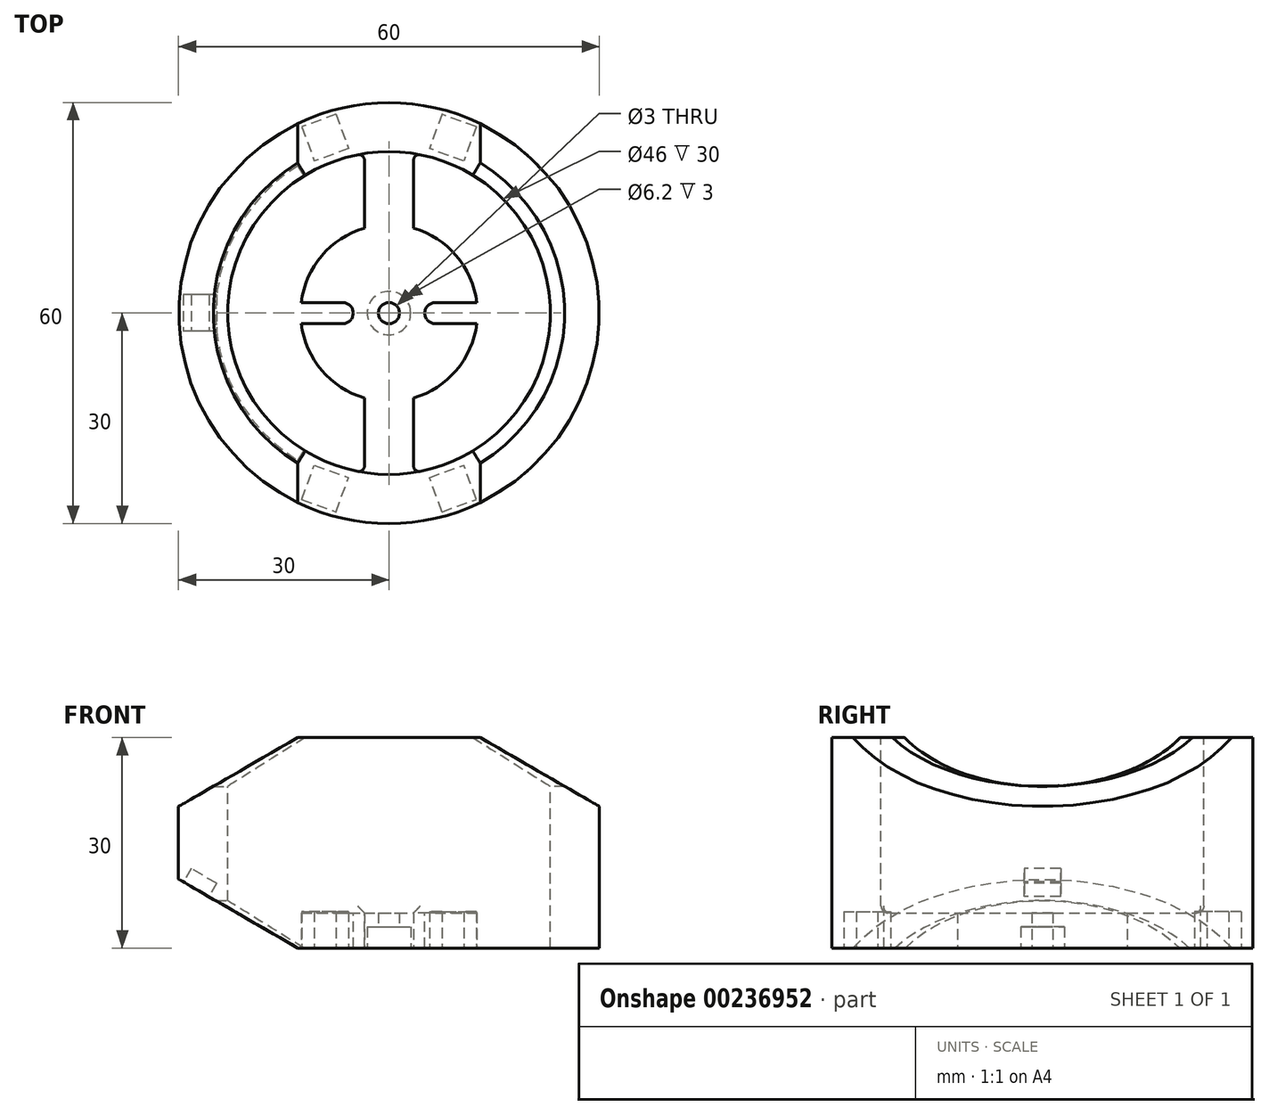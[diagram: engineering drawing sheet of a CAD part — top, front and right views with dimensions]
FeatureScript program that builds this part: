
annotation { "Feature Type Name" : "Feature", "Feature Type Description" : "" }
export const myFeature = defineFeature(function(context is Context, id is Id, definition is map)
    precondition{}
    {
        {
            var Q0;
            Q0=qCreatedBy(makeId("Top.planeOp"),FACE);
            var sketch = newSketch(context, id + "F0", { "sketchPlane" : qUnion([Q0])});
            skCircle(sketch, "E0", {"center": v(0, 0) * mm, "radius": 30 * mm});
            skSolve(sketch);
        }
        {
            var Q0;
            Q0 = qSketchRegion(id + "F0", true);
            extrude(context, id + "F1", {"entities" : qUnion([Q0]), "depth" : 30 * mm});
        }
        {
            var Q0;
            Q0=qCreatedBy(makeId("Front.planeOp"),FACE);
            var sketch = newSketch(context, id + "F2", { "sketchPlane" : qUnion([Q0])});
            skLineSegment(sketch, "E1", {"start": v(-30, 0) * mm, "end": v(-30, 30) * mm});
            skLineSegment(sketch, "E2.0", {"start": v(-30, 0) * mm, "end": v(30, 0) * mm});
            skLineSegment(sketch, "E3", {"start": v(-30, 9.81) * mm, "end": v(-13, 0) * mm});
            skSolve(sketch);
        }
        {
            var Q0;
            Q0 = qSketchRegion(id + "F2", true);
            extrude(context, id + "F3", {"entities" : qUnion([Q0]), "operationType" : NewBodyOperationType.REMOVE, "oppositeDirection" : true, "depth" : 40 * mm, "hasSecondDirection" : true, "secondDirectionOppositeDirection" : false, "secondDirectionDepth" : 40 * mm});
        }
        {
            var Q0;
            Q0=makeQuery(id+"F1.opExtrude","CAP_FACE",FACE,{"disambiguationData":[OSD([sQuery(id+"F0.wireOp",EDGE,"E0")])],"isStart":false});
            var sketch = newSketch(context, id + "F4", { "sketchPlane" : qUnion([Q0])});
            skCircle(sketch, "E4", {"center": v(0, 0) * mm, "radius": 23 * mm});
            skSolve(sketch);
        }
        {
            var Q0;
            Q0 = qSketchRegion(id + "F4", true);
            extrude(context, id + "F5", {"entities" : qUnion([Q0]), "operationType" : NewBodyOperationType.REMOVE, "oppositeDirection" : true, "depth" : 40 * mm});
        }
        {
            var Q0;
            Q0=makeQuery(id+"F5.boolean.opBoolean","SPLIT",FACE,{"disambiguationData":[OD(0.0)],"derivedFrom":makeQuery(id+"F1.opExtrude","CAP_FACE",FACE,{"disambiguationData":[OSD([sQuery(id+"F0.wireOp",EDGE,"E0")])],"isStart":true})});
            var sketch = newSketch(context, id + "F6", { "sketchPlane" : qUnion([Q0])});
            skCircle(sketch, "E5", {"center": v(0, 0) * mm, "radius": 12.6 * mm});
            skLineSegment(sketch, "E6.bottom", {"start": v(3.5, 25) * mm, "end": v(-3.5, 25) * mm});
            skLineSegment(sketch, "E6.top", {"start": v(3.5, -25) * mm, "end": v(-3.5, -25) * mm});
            skLineSegment(sketch, "E6.left", {"start": v(3.5, 25) * mm, "end": v(3.5, -25) * mm});
            skLineSegment(sketch, "E6.right", {"start": v(-3.5, 25) * mm, "end": v(-3.5, -25) * mm});
            skSolve(sketch);
        }
        {
            var Q0;
            Q0 = qSketchRegion(id + "F6", true);
            extrude(context, id + "F7", {"entities" : qUnion([Q0]), "operationType" : NewBodyOperationType.ADD, "oppositeDirection" : true, "depth" : 5 * mm});
        }
        {
            var Q0;
            {var subQ0=makeQuery(id+"F1.opExtrude","CAP_FACE",FACE,{"disambiguationData":[OSD([sQuery(id+"F0.wireOp",EDGE,"E0")])],"isStart":true});Q0=makeQuery(id+"F7.boolean.opBoolean","MERGE",FACE,{"derivedFrom":[makeQuery(id+"F5.boolean.opBoolean","SPLIT",FACE,{"disambiguationData":[OD(0.0)],"derivedFrom":subQ0}),makeQuery(id+"F5.boolean.opBoolean","SPLIT",FACE,{"disambiguationData":[OD(1.0)],"derivedFrom":subQ0}),makeQuery(id+"F7.opExtrude","CAP_FACE",FACE,{"disambiguationData":[OSD([sQuery(id+"F6.wireOp",EDGE,"E5"),sQuery(id+"F6.wireOp",EDGE,"E6.bottom"),sQuery(id+"F6.wireOp",EDGE,"E6.top"),sQuery(id+"F6.wireOp",EDGE,"E6.left"),sQuery(id+"F6.wireOp",EDGE,"E6.right")])],"isStart":true})]});}
            var sketch = newSketch(context, id + "F8", { "sketchPlane" : qUnion([Q0])});
            skCircle(sketch, "E7", {"center": v(0, 0) * mm, "radius": 1.5 * mm});
            skSolve(sketch);
        }
        {
            var Q0;
            Q0 = qSketchRegion(id + "F8", true);
            extrude(context, id + "F9", {"entities" : qUnion([Q0]), "operationType" : NewBodyOperationType.REMOVE, "oppositeDirection" : true, "depth" : 25 * mm});
        }
        {
            var Q0;
            {var subQ0=makeQuery(id+"F1.opExtrude","CAP_FACE",FACE,{"disambiguationData":[OSD([sQuery(id+"F0.wireOp",EDGE,"E0")])],"isStart":true});Q0=makeQuery(id+"F7.boolean.opBoolean","MERGE",FACE,{"derivedFrom":[makeQuery(id+"F5.boolean.opBoolean","SPLIT",FACE,{"disambiguationData":[OD(0.0)],"derivedFrom":subQ0}),makeQuery(id+"F5.boolean.opBoolean","SPLIT",FACE,{"disambiguationData":[OD(1.0)],"derivedFrom":subQ0}),makeQuery(id+"F7.opExtrude","CAP_FACE",FACE,{"disambiguationData":[OSD([sQuery(id+"F6.wireOp",EDGE,"E5"),sQuery(id+"F6.wireOp",EDGE,"E6.bottom"),sQuery(id+"F6.wireOp",EDGE,"E6.top"),sQuery(id+"F6.wireOp",EDGE,"E6.left"),sQuery(id+"F6.wireOp",EDGE,"E6.right")])],"isStart":true})]});}
            var sketch = newSketch(context, id + "F10", { "sketchPlane" : qUnion([Q0])});
            skCircle(sketch, "E8", {"center": v(0, 0) * mm, "radius": 3.1 * mm});
            skSolve(sketch);
        }
        {
            var Q0;
            Q0 = qSketchRegion(id + "F10", true);
            extrude(context, id + "F11", {"entities" : qUnion([Q0]), "operationType" : NewBodyOperationType.REMOVE, "oppositeDirection" : true, "depth" : 3 * mm});
        }
        {
            var Q0;
            {var subQ0=makeQuery(id+"F1.opExtrude","CAP_FACE",FACE,{"disambiguationData":[OSD([sQuery(id+"F0.wireOp",EDGE,"E0")])],"isStart":true});Q0=makeQuery(id+"F7.boolean.opBoolean","MERGE",FACE,{"derivedFrom":[makeQuery(id+"F5.boolean.opBoolean","SPLIT",FACE,{"disambiguationData":[OD(0.0)],"derivedFrom":subQ0}),makeQuery(id+"F5.boolean.opBoolean","SPLIT",FACE,{"disambiguationData":[OD(1.0)],"derivedFrom":subQ0}),makeQuery(id+"F7.opExtrude","CAP_FACE",FACE,{"disambiguationData":[OSD([sQuery(id+"F6.wireOp",EDGE,"E5"),sQuery(id+"F6.wireOp",EDGE,"E6.bottom"),sQuery(id+"F6.wireOp",EDGE,"E6.top"),sQuery(id+"F6.wireOp",EDGE,"E6.left"),sQuery(id+"F6.wireOp",EDGE,"E6.right")])],"isStart":true})]});}
            var sketch = newSketch(context, id + "F12", { "sketchPlane" : qUnion([Q0])});
            skLineSegment(sketch, "E9.bottom", {"start": v(-5.1, -1.5) * mm, "end": v(-20.1, -1.5) * mm});
            skLineSegment(sketch, "E9.top", {"start": v(-5.1, 1.5) * mm, "end": v(-20.1, 1.5) * mm});
            skLineSegment(sketch, "E9.left", {"start": v(-5.1, -1.5) * mm, "end": v(-5.1, 1.5) * mm});
            skLineSegment(sketch, "E9.right", {"start": v(-20.1, -1.5) * mm, "end": v(-20.1, 1.5) * mm});
            skPoint(sketch, "E9.middle", {"position": v(-12.6, 0) * mm});
            skLineSegment(sketch, "E10.bottom", {"start": v(5.1, -1.5) * mm, "end": v(20.1, -1.5) * mm});
            skLineSegment(sketch, "E10.top", {"start": v(5.1, 1.5) * mm, "end": v(20.1, 1.5) * mm});
            skLineSegment(sketch, "E10.left", {"start": v(5.1, -1.5) * mm, "end": v(5.1, 1.5) * mm});
            skLineSegment(sketch, "E10.right", {"start": v(20.1, -1.5) * mm, "end": v(20.1, 1.5) * mm});
            skPoint(sketch, "E10.middle", {"position": v(12.6, 0) * mm});
            skSolve(sketch);
        }
        {
            var Q0;
            Q0 = qSketchRegion(id + "F12", true);
            extrude(context, id + "F13", {"entities" : qUnion([Q0]), "operationType" : NewBodyOperationType.REMOVE, "oppositeDirection" : true, "depth" : 25 * mm});
        }
        {
            var Q0;
            Q0=makeQuery(id+"F13.boolean.opBoolean","COPY",EDGE,{"derivedFrom":makeQuery(id+"F13.opExtrude","SWEPT_EDGE",EDGE,{"disambiguationData":[OSD([sQuery(id+"F12.wireOp",EDGE,"E9.top"),sQuery(id+"F12.wireOp",EDGE,"E9.left")])]})});
            var Q1;
            Q1=makeQuery(id+"F13.boolean.opBoolean","COPY",EDGE,{"derivedFrom":makeQuery(id+"F13.opExtrude","SWEPT_EDGE",EDGE,{"disambiguationData":[OSD([sQuery(id+"F12.wireOp",EDGE,"E10.top"),sQuery(id+"F12.wireOp",EDGE,"E10.left")])]})});
            var Q2;
            Q2=makeQuery(id+"F13.boolean.opBoolean","COPY",EDGE,{"derivedFrom":makeQuery(id+"F13.opExtrude","SWEPT_EDGE",EDGE,{"disambiguationData":[OSD([sQuery(id+"F12.wireOp",EDGE,"E10.bottom"),sQuery(id+"F12.wireOp",EDGE,"E10.left")])]})});
            var Q3;
            Q3=makeQuery(id+"F13.boolean.opBoolean","COPY",EDGE,{"derivedFrom":makeQuery(id+"F13.opExtrude","SWEPT_EDGE",EDGE,{"disambiguationData":[OSD([sQuery(id+"F12.wireOp",EDGE,"E9.bottom"),sQuery(id+"F12.wireOp",EDGE,"E9.left")])]})});
            fillet(context, id + "F14", {"entities" : qUnion([Q0, Q1, Q2, Q3]), "radius" : 1.5 * mm, "tangentPropagation" : true, "allowEdgeOverflow" : false});
        }
        {
            var Q0;
            Q0=makeQuery(id+"F5.boolean.opBoolean","INTERSECT",EDGE,{"derivedFrom":[makeQuery(id+"F3.boolean.opBoolean","COPY",FACE,{"derivedFrom":makeQuery(id+"F3.opExtrude","SWEPT_FACE",FACE,{"disambiguationData":[OSD([sQuery(id+"F2.wireOp",EDGE,"E3")])]})}),makeQuery(id+"F5.opExtrude","SWEPT_FACE",FACE,{"disambiguationData":[OSD([sQuery(id+"F4.wireOp",EDGE,"E4")])]})]});
            var Q1;
            Q1=makeQuery(id+"F5.boolean.opBoolean","INTERSECT",EDGE,{"derivedFrom":[makeQuery(id+"FJe8OaDZyjXPkyk_1.1.F3.boolean.opBoolean","COPY",FACE,{"derivedFrom":makeQuery(id+"FJe8OaDZyjXPkyk_1.1.F3.opExtrude","SWEPT_FACE",FACE,{"disambiguationData":[OSD([sQuery(id+"F2.wireOp",EDGE,"E3")])]})}),makeQuery(id+"F5.opExtrude","SWEPT_FACE",FACE,{"disambiguationData":[OSD([sQuery(id+"F4.wireOp",EDGE,"E4")])]})]});
            chamfer(context, id + "F15", {"entities" : qUnion([Q0, Q1]), "chamferType" : ChamferType.OFFSET_ANGLE, "width" : 0.5 * mm, "oppositeDirection" : false, "angle" : 90 * degree, "tangentPropagation" : true});
        }
        {
            var Q0;
            Q0=qCreatedBy(makeId("Front.planeOp"),FACE);
            var sketch = newSketch(context, id + "F16", { "sketchPlane" : qUnion([Q0])});
            skLineSegment(sketch, "E11", {"start": v(-30, 10.4) * mm, "end": v(-30, 30) * mm});
            skLineSegment(sketch, "E12.0", {"start": v(-30, 30) * mm, "end": v(30, 30) * mm});
            skLineSegment(sketch, "E13", {"start": v(30, 30) * mm, "end": v(30, 10.4) * mm});
            skLineSegment(sketch, "E14", {"start": v(-30, 20.19) * mm, "end": v(-13, 30) * mm});
            skLineSegment(sketch, "E15", {"start": v(13, 30) * mm, "end": v(30, 20.19) * mm});
            skSolve(sketch);
        }
        {
            var Q0;
            Q0 = qSketchRegion(id + "F16", true);
            extrude(context, id + "F17", {"entities" : qUnion([Q0]), "operationType" : NewBodyOperationType.REMOVE, "oppositeDirection" : true, "depth" : 40 * mm, "hasSecondDirection" : true, "secondDirectionOppositeDirection" : false, "secondDirectionDepth" : 40 * mm});
        }
        {
            var Q0;
            {var subQ0=sQuery(id+"F6.wireOp",EDGE,"E6.right");var subQ1=makeQuery(id+"F5.opExtrude","SWEPT_FACE",FACE,{"disambiguationData":[OSD([sQuery(id+"F4.wireOp",EDGE,"E4")])]});Q0=makeQuery(id+"F7.boolean.opBoolean","INTERSECT",EDGE,{"derivedFrom":[makeQuery(id+"F5.boolean.opBoolean","COPY",FACE,{"derivedFrom":subQ1}),makeQuery(id+"F7.opExtrude","SWEPT_FACE",FACE,{"disambiguationData":[OSD([subQ0]),TDD([makeQuery(id+"F6.imprint","IMPRINT",EDGE,{"disambiguationData":[TD([[makeQuery(id+"F6.imprint","INTERSECT",VERTEX,{"derivedFrom":[sQuery(id+"F6.wireOp",EDGE,"E6.bottom"),subQ0]}),-1.0]])],"derivedFrom":subQ0}),makeQuery(id+"F6.imprint","IMPRINT",EDGE,{"disambiguationData":[TD([[makeQuery(id+"F6.imprint","INTERSECT",VERTEX,{"disambiguationData":[OD(0.0)],"derivedFrom":[sQuery(id+"F6.wireOp",EDGE,"E5"),subQ0]}),1.0]])],"derivedFrom":subQ0})])]})]});}
            var Q1;
            {var subQ0=sQuery(id+"F6.wireOp",EDGE,"E6.left");var subQ1=makeQuery(id+"F5.opExtrude","SWEPT_FACE",FACE,{"disambiguationData":[OSD([sQuery(id+"F4.wireOp",EDGE,"E4")])]});Q1=makeQuery(id+"F7.boolean.opBoolean","INTERSECT",EDGE,{"derivedFrom":[makeQuery(id+"F5.boolean.opBoolean","COPY",FACE,{"derivedFrom":subQ1}),makeQuery(id+"F7.opExtrude","SWEPT_FACE",FACE,{"disambiguationData":[OSD([subQ0]),TDD([makeQuery(id+"F6.imprint","IMPRINT",EDGE,{"disambiguationData":[TD([[makeQuery(id+"F6.imprint","INTERSECT",VERTEX,{"derivedFrom":[sQuery(id+"F6.wireOp",EDGE,"E6.bottom"),subQ0]}),-1.0]])],"derivedFrom":subQ0}),makeQuery(id+"F6.imprint","IMPRINT",EDGE,{"disambiguationData":[TD([[makeQuery(id+"F6.imprint","INTERSECT",VERTEX,{"disambiguationData":[OD(0.0)],"derivedFrom":[sQuery(id+"F6.wireOp",EDGE,"E5"),subQ0]}),1.0]])],"derivedFrom":subQ0})])]})]});}
            var Q2;
            {var subQ0=sQuery(id+"F6.wireOp",EDGE,"E6.left");Q2=makeQuery(id+"F7.boolean.opBoolean","INTERSECT",EDGE,{"derivedFrom":[makeQuery(id+"F5.boolean.opBoolean","COPY",FACE,{"derivedFrom":makeQuery(id+"F5.opExtrude","SWEPT_FACE",FACE,{"disambiguationData":[OSD([sQuery(id+"F4.wireOp",EDGE,"E4")])]})}),makeQuery(id+"F7.opExtrude","SWEPT_FACE",FACE,{"disambiguationData":[OSD([subQ0]),TDD([makeQuery(id+"F6.imprint","IMPRINT",EDGE,{"disambiguationData":[TD([[makeQuery(id+"F6.imprint","INTERSECT",VERTEX,{"derivedFrom":[sQuery(id+"F6.wireOp",EDGE,"E6.top"),subQ0]}),1.0]])],"derivedFrom":subQ0})])]})]});}
            var Q3;
            {var subQ0=sQuery(id+"F6.wireOp",EDGE,"E6.right");Q3=makeQuery(id+"F7.boolean.opBoolean","INTERSECT",EDGE,{"derivedFrom":[makeQuery(id+"F5.boolean.opBoolean","COPY",FACE,{"derivedFrom":makeQuery(id+"F5.opExtrude","SWEPT_FACE",FACE,{"disambiguationData":[OSD([sQuery(id+"F4.wireOp",EDGE,"E4")])]})}),makeQuery(id+"F7.opExtrude","SWEPT_FACE",FACE,{"disambiguationData":[OSD([subQ0]),TDD([makeQuery(id+"F6.imprint","IMPRINT",EDGE,{"disambiguationData":[TD([[makeQuery(id+"F6.imprint","INTERSECT",VERTEX,{"derivedFrom":[sQuery(id+"F6.wireOp",EDGE,"E6.top"),subQ0]}),1.0]])],"derivedFrom":subQ0})])]})]});}
            fillet(context, id + "F18", {"entities" : qUnion([Q0, Q1, Q2, Q3]), "radius" : 0.8 * mm, "tangentPropagation" : true, "allowEdgeOverflow" : false});
        }
        {
            var Q0;
            {var subQ0=makeQuery(id+"F1.opExtrude","CAP_FACE",FACE,{"disambiguationData":[OSD([sQuery(id+"F0.wireOp",EDGE,"E0")])],"isStart":true});Q0=makeQuery(id+"F7.boolean.opBoolean","MERGE",FACE,{"derivedFrom":[makeQuery(id+"F5.boolean.opBoolean","SPLIT",FACE,{"disambiguationData":[OD(0.0)],"derivedFrom":subQ0}),makeQuery(id+"F5.boolean.opBoolean","SPLIT",FACE,{"disambiguationData":[OD(1.0)],"derivedFrom":subQ0}),makeQuery(id+"F7.opExtrude","CAP_FACE",FACE,{"disambiguationData":[OSD([sQuery(id+"F6.wireOp",EDGE,"E5"),sQuery(id+"F6.wireOp",EDGE,"E6.bottom"),sQuery(id+"F6.wireOp",EDGE,"E6.top"),sQuery(id+"F6.wireOp",EDGE,"E6.left"),sQuery(id+"F6.wireOp",EDGE,"E6.right")])],"isStart":true})]});}
            var sketch = newSketch(context, id + "F19", { "sketchPlane" : qUnion([Q0])});
            skLineSegment(sketch, "E16.bottom", {"start": v(2.6, -29.2) * mm, "end": v(-2.6, -29.2) * mm});
            skLineSegment(sketch, "E16.top", {"start": v(2.6, -24) * mm, "end": v(-2.6, -24) * mm});
            skLineSegment(sketch, "E16.left", {"start": v(2.6, -29.2) * mm, "end": v(2.6, -24) * mm});
            skLineSegment(sketch, "E16.right", {"start": v(-2.6, -29.2) * mm, "end": v(-2.6, -24) * mm});
            skPoint(sketch, "E16.middle", {"position": v(0, -26.6) * mm});
            skPoint(sketch, "E16.middle.positionSnap0", {"position": v(0, -30) * mm});
            skPoint(sketch, "E16.centerSnap0", {"position": v(0, -30) * mm});
            skLineSegment(sketch, "E17.1.0", {"start": v(7.54, -28.33) * mm, "end": v(5.77, -23.44) * mm});
            skLineSegment(sketch, "E17.1.1", {"start": v(10.65, -21.66) * mm, "end": v(5.77, -23.44) * mm});
            skLineSegment(sketch, "E17.1.2", {"start": v(12.43, -26.55) * mm, "end": v(10.65, -21.66) * mm});
            skLineSegment(sketch, "E17.1.3", {"start": v(12.43, -26.55) * mm, "end": v(7.54, -28.33) * mm});
            skLineSegment(sketch, "E17.2.0", {"start": v(16.78, -24.04) * mm, "end": v(13.44, -20.06) * mm});
            skLineSegment(sketch, "E17.2.1", {"start": v(17.42, -16.71) * mm, "end": v(13.44, -20.06) * mm});
            skLineSegment(sketch, "E17.2.2", {"start": v(20.76, -20.7) * mm, "end": v(17.42, -16.71) * mm});
            skLineSegment(sketch, "E17.2.3", {"start": v(20.76, -20.7) * mm, "end": v(16.78, -24.04) * mm});
            skLineSegment(sketch, "E17.3.0", {"start": v(23.99, -16.85) * mm, "end": v(19.48, -14.25) * mm});
            skLineSegment(sketch, "E17.3.1", {"start": v(22.08, -9.75) * mm, "end": v(19.48, -14.25) * mm});
            skLineSegment(sketch, "E17.3.2", {"start": v(26.59, -12.35) * mm, "end": v(22.08, -9.75) * mm});
            skLineSegment(sketch, "E17.3.3", {"start": v(26.59, -12.35) * mm, "end": v(23.99, -16.85) * mm});
            skLineSegment(sketch, "E17.4.0", {"start": v(28.3, -7.63) * mm, "end": v(23.18, -6.73) * mm});
            skLineSegment(sketch, "E17.4.1", {"start": v(24.09, -1.6) * mm, "end": v(23.18, -6.73) * mm});
            skLineSegment(sketch, "E17.4.2", {"start": v(29.2, -2.51) * mm, "end": v(24.09, -1.6) * mm});
            skLineSegment(sketch, "E17.4.3", {"start": v(29.2, -2.51) * mm, "end": v(28.3, -7.63) * mm});
            skLineSegment(sketch, "E17.5.0", {"start": v(29.2, 2.51) * mm, "end": v(24.09, 1.6) * mm});
            skLineSegment(sketch, "E17.5.1", {"start": v(23.18, 6.73) * mm, "end": v(24.09, 1.6) * mm});
            skLineSegment(sketch, "E17.5.2", {"start": v(28.3, 7.63) * mm, "end": v(23.18, 6.73) * mm});
            skLineSegment(sketch, "E17.5.3", {"start": v(28.3, 7.63) * mm, "end": v(29.2, 2.51) * mm});
            skLineSegment(sketch, "E17.6.0", {"start": v(26.59, 12.35) * mm, "end": v(22.08, 9.75) * mm});
            skLineSegment(sketch, "E17.6.1", {"start": v(19.48, 14.25) * mm, "end": v(22.08, 9.75) * mm});
            skLineSegment(sketch, "E17.6.2", {"start": v(23.99, 16.85) * mm, "end": v(19.48, 14.25) * mm});
            skLineSegment(sketch, "E17.6.3", {"start": v(23.99, 16.85) * mm, "end": v(26.59, 12.35) * mm});
            skLineSegment(sketch, "E17.7.0", {"start": v(20.76, 20.7) * mm, "end": v(17.42, 16.71) * mm});
            skLineSegment(sketch, "E17.7.1", {"start": v(13.44, 20.06) * mm, "end": v(17.42, 16.71) * mm});
            skLineSegment(sketch, "E17.7.2", {"start": v(16.78, 24.04) * mm, "end": v(13.44, 20.06) * mm});
            skLineSegment(sketch, "E17.7.3", {"start": v(16.78, 24.04) * mm, "end": v(20.76, 20.7) * mm});
            skLineSegment(sketch, "E17.8.0", {"start": v(12.43, 26.55) * mm, "end": v(10.65, 21.66) * mm});
            skLineSegment(sketch, "E17.8.1", {"start": v(5.77, 23.44) * mm, "end": v(10.65, 21.66) * mm});
            skLineSegment(sketch, "E17.8.2", {"start": v(7.54, 28.33) * mm, "end": v(5.77, 23.44) * mm});
            skLineSegment(sketch, "E17.8.3", {"start": v(7.54, 28.33) * mm, "end": v(12.43, 26.55) * mm});
            skLineSegment(sketch, "E17.9.0", {"start": v(2.6, 29.2) * mm, "end": v(2.6, 24) * mm});
            skLineSegment(sketch, "E17.9.1", {"start": v(-2.6, 24) * mm, "end": v(2.6, 24) * mm});
            skLineSegment(sketch, "E17.9.2", {"start": v(-2.6, 29.2) * mm, "end": v(-2.6, 24) * mm});
            skLineSegment(sketch, "E17.9.3", {"start": v(-2.6, 29.2) * mm, "end": v(2.6, 29.2) * mm});
            skLineSegment(sketch, "E17.10.0", {"start": v(-7.54, 28.33) * mm, "end": v(-5.77, 23.44) * mm});
            skLineSegment(sketch, "E17.10.1", {"start": v(-10.65, 21.66) * mm, "end": v(-5.77, 23.44) * mm});
            skLineSegment(sketch, "E17.10.2", {"start": v(-12.43, 26.55) * mm, "end": v(-10.65, 21.66) * mm});
            skLineSegment(sketch, "E17.10.3", {"start": v(-12.43, 26.55) * mm, "end": v(-7.54, 28.33) * mm});
            skLineSegment(sketch, "E17.11.0", {"start": v(-16.78, 24.04) * mm, "end": v(-13.44, 20.06) * mm});
            skLineSegment(sketch, "E17.11.1", {"start": v(-17.42, 16.71) * mm, "end": v(-13.44, 20.06) * mm});
            skLineSegment(sketch, "E17.11.2", {"start": v(-20.76, 20.7) * mm, "end": v(-17.42, 16.71) * mm});
            skLineSegment(sketch, "E17.11.3", {"start": v(-20.76, 20.7) * mm, "end": v(-16.78, 24.04) * mm});
            skLineSegment(sketch, "E17.12.0", {"start": v(-23.99, 16.85) * mm, "end": v(-19.48, 14.25) * mm});
            skLineSegment(sketch, "E17.12.1", {"start": v(-22.08, 9.75) * mm, "end": v(-19.48, 14.25) * mm});
            skLineSegment(sketch, "E17.12.2", {"start": v(-26.59, 12.35) * mm, "end": v(-22.08, 9.75) * mm});
            skLineSegment(sketch, "E17.12.3", {"start": v(-26.59, 12.35) * mm, "end": v(-23.99, 16.85) * mm});
            skLineSegment(sketch, "E17.13.0", {"start": v(-28.3, 7.63) * mm, "end": v(-23.18, 6.73) * mm});
            skLineSegment(sketch, "E17.13.1", {"start": v(-24.09, 1.6) * mm, "end": v(-23.18, 6.73) * mm});
            skLineSegment(sketch, "E17.13.2", {"start": v(-29.2, 2.51) * mm, "end": v(-24.09, 1.6) * mm});
            skLineSegment(sketch, "E17.13.3", {"start": v(-29.2, 2.51) * mm, "end": v(-28.3, 7.63) * mm});
            skLineSegment(sketch, "E17.14.0", {"start": v(-29.2, -2.51) * mm, "end": v(-24.09, -1.6) * mm});
            skLineSegment(sketch, "E17.14.1", {"start": v(-23.18, -6.73) * mm, "end": v(-24.09, -1.6) * mm});
            skLineSegment(sketch, "E17.14.2", {"start": v(-28.3, -7.63) * mm, "end": v(-23.18, -6.73) * mm});
            skLineSegment(sketch, "E17.14.3", {"start": v(-28.3, -7.63) * mm, "end": v(-29.2, -2.51) * mm});
            skLineSegment(sketch, "E17.15.0", {"start": v(-26.59, -12.35) * mm, "end": v(-22.08, -9.75) * mm});
            skLineSegment(sketch, "E17.15.1", {"start": v(-19.48, -14.25) * mm, "end": v(-22.08, -9.75) * mm});
            skLineSegment(sketch, "E17.15.2", {"start": v(-23.99, -16.85) * mm, "end": v(-19.48, -14.25) * mm});
            skLineSegment(sketch, "E17.15.3", {"start": v(-23.99, -16.85) * mm, "end": v(-26.59, -12.35) * mm});
            skLineSegment(sketch, "E17.16.0", {"start": v(-20.76, -20.7) * mm, "end": v(-17.42, -16.71) * mm});
            skLineSegment(sketch, "E17.16.1", {"start": v(-13.44, -20.06) * mm, "end": v(-17.42, -16.71) * mm});
            skLineSegment(sketch, "E17.16.2", {"start": v(-16.78, -24.04) * mm, "end": v(-13.44, -20.06) * mm});
            skLineSegment(sketch, "E17.16.3", {"start": v(-16.78, -24.04) * mm, "end": v(-20.76, -20.7) * mm});
            skLineSegment(sketch, "E17.17.0", {"start": v(-12.43, -26.55) * mm, "end": v(-10.65, -21.66) * mm});
            skLineSegment(sketch, "E17.17.1", {"start": v(-5.77, -23.44) * mm, "end": v(-10.65, -21.66) * mm});
            skLineSegment(sketch, "E17.17.2", {"start": v(-7.54, -28.33) * mm, "end": v(-5.77, -23.44) * mm});
            skLineSegment(sketch, "E17.17.3", {"start": v(-7.54, -28.33) * mm, "end": v(-12.43, -26.55) * mm});
            skPoint(sketch, "E17.center", {"position": v(0, 0) * mm});
            skSolve(sketch);
        }
        {
            var Q0;
            Q0=makeQuery(id+"F19.imprint","IMPRINT",FACE,{"disambiguationData":[TD([[makeQuery(id+"F19.imprint","IMPRINT",EDGE,{"derivedFrom":sQuery(id+"F19.wireOp",EDGE,"E17.17.0")}),-1.0]])]});
            var Q1;
            Q1=makeQuery(id+"F19.imprint","IMPRINT",FACE,{"disambiguationData":[TD([[makeQuery(id+"F19.imprint","IMPRINT",EDGE,{"derivedFrom":sQuery(id+"F19.wireOp",EDGE,"E17.1.0")}),-1.0]])]});
            var Q2;
            Q2=makeQuery(id+"F19.imprint","IMPRINT",FACE,{"disambiguationData":[TD([[makeQuery(id+"F19.imprint","IMPRINT",EDGE,{"derivedFrom":sQuery(id+"F19.wireOp",EDGE,"E17.10.0")}),-1.0]])]});
            var Q3;
            Q3=makeQuery(id+"F19.imprint","IMPRINT",FACE,{"disambiguationData":[TD([[makeQuery(id+"F19.imprint","IMPRINT",EDGE,{"derivedFrom":sQuery(id+"F19.wireOp",EDGE,"E17.8.0")}),-1.0]])]});
            extrude(context, id + "F20", {"entities" : qUnion([Q0, Q1, Q2, Q3]), "operationType" : NewBodyOperationType.REMOVE, "oppositeDirection" : true, "depth" : 5.2 * mm});
        }
        {
            var Q0;
            Q0=makeQuery(id+"F7.boolean.opBoolean","INTERSECT",EDGE,{"disambiguationData":[OD(1.0)],"derivedFrom":[makeQuery(id+"F5.boolean.opBoolean","COPY",FACE,{"derivedFrom":makeQuery(id+"F5.opExtrude","SWEPT_FACE",FACE,{"disambiguationData":[OSD([sQuery(id+"F4.wireOp",EDGE,"E4")])]})}),makeQuery(id+"F7.opExtrude","CAP_FACE",FACE,{"disambiguationData":[OSD([sQuery(id+"F6.wireOp",EDGE,"E5"),sQuery(id+"F6.wireOp",EDGE,"E6.bottom"),sQuery(id+"F6.wireOp",EDGE,"E6.top"),sQuery(id+"F6.wireOp",EDGE,"E6.left"),sQuery(id+"F6.wireOp",EDGE,"E6.right")])],"isStart":false})]});
            var Q1;
            Q1=makeQuery(id+"F7.boolean.opBoolean","INTERSECT",EDGE,{"disambiguationData":[OD(0.0)],"derivedFrom":[makeQuery(id+"F5.boolean.opBoolean","COPY",FACE,{"derivedFrom":makeQuery(id+"F5.opExtrude","SWEPT_FACE",FACE,{"disambiguationData":[OSD([sQuery(id+"F4.wireOp",EDGE,"E4")])]})}),makeQuery(id+"F7.opExtrude","CAP_FACE",FACE,{"disambiguationData":[OSD([sQuery(id+"F6.wireOp",EDGE,"E5"),sQuery(id+"F6.wireOp",EDGE,"E6.bottom"),sQuery(id+"F6.wireOp",EDGE,"E6.top"),sQuery(id+"F6.wireOp",EDGE,"E6.left"),sQuery(id+"F6.wireOp",EDGE,"E6.right")])],"isStart":false})]});
            fillet(context, id + "F21", {"entities" : qUnion([Q0, Q1]), "radius" : 1 * mm, "tangentPropagation" : true, "allowEdgeOverflow" : false});
        }
        {
            var Q0;
            Q0=makeQuery(id+"F17.boolean.opBoolean","INTERSECT",EDGE,{"derivedFrom":[makeQuery(id+"F5.boolean.opBoolean","COPY",FACE,{"derivedFrom":makeQuery(id+"F5.opExtrude","SWEPT_FACE",FACE,{"disambiguationData":[OSD([sQuery(id+"F4.wireOp",EDGE,"E4")])]})}),makeQuery(id+"F17.opExtrude","SWEPT_FACE",FACE,{"disambiguationData":[OSD([sQuery(id+"F16.wireOp",EDGE,"E15")])]})]});
            var Q1;
            Q1=makeQuery(id+"F17.boolean.opBoolean","INTERSECT",EDGE,{"derivedFrom":[makeQuery(id+"F5.boolean.opBoolean","COPY",FACE,{"derivedFrom":makeQuery(id+"F5.opExtrude","SWEPT_FACE",FACE,{"disambiguationData":[OSD([sQuery(id+"F4.wireOp",EDGE,"E4")])]})}),makeQuery(id+"F17.opExtrude","SWEPT_FACE",FACE,{"disambiguationData":[OSD([sQuery(id+"F16.wireOp",EDGE,"E14")])]})]});
            chamfer(context, id + "F22", {"entities" : qUnion([Q0, Q1]), "chamferType" : ChamferType.OFFSET_ANGLE, "width" : 0.6 * mm, "oppositeDirection" : false, "angle" : 90 * degree, "tangentPropagation" : true});
        }
        {
            var Q0;
            Q0=makeQuery(id+"F3.boolean.opBoolean","COPY",FACE,{"derivedFrom":makeQuery(id+"F3.opExtrude","SWEPT_FACE",FACE,{"disambiguationData":[OSD([sQuery(id+"F2.wireOp",EDGE,"E3")])]})});
            var sketch = newSketch(context, id + "F23", { "sketchPlane" : qUnion([Q0])});
            skLineSegment(sketch, "E18.bottom", {"start": v(-25.89, -2.6) * mm, "end": v(-30.09, -2.6) * mm});
            skLineSegment(sketch, "E18.top", {"start": v(-25.89, 2.6) * mm, "end": v(-30.09, 2.6) * mm});
            skLineSegment(sketch, "E18.left", {"start": v(-25.89, -2.6) * mm, "end": v(-25.89, 2.6) * mm});
            skLineSegment(sketch, "E18.right", {"start": v(-30.09, -2.6) * mm, "end": v(-30.09, 2.6) * mm});
            skPoint(sketch, "E18.middle", {"position": v(-27.99, 0) * mm});
            skPoint(sketch, "E18.middle.positionSnap0", {"position": v(-30.89, 0) * mm});
            skPoint(sketch, "E18.centerSnap0", {"position": v(-30.89, 0) * mm});
            skSolve(sketch);
        }
        {
            var Q0;
            Q0 = qSketchRegion(id + "F23", true);
            extrude(context, id + "F24", {"entities" : qUnion([Q0]), "operationType" : NewBodyOperationType.REMOVE, "oppositeDirection" : true, "depth" : 2.2 * mm});
        }
    });
